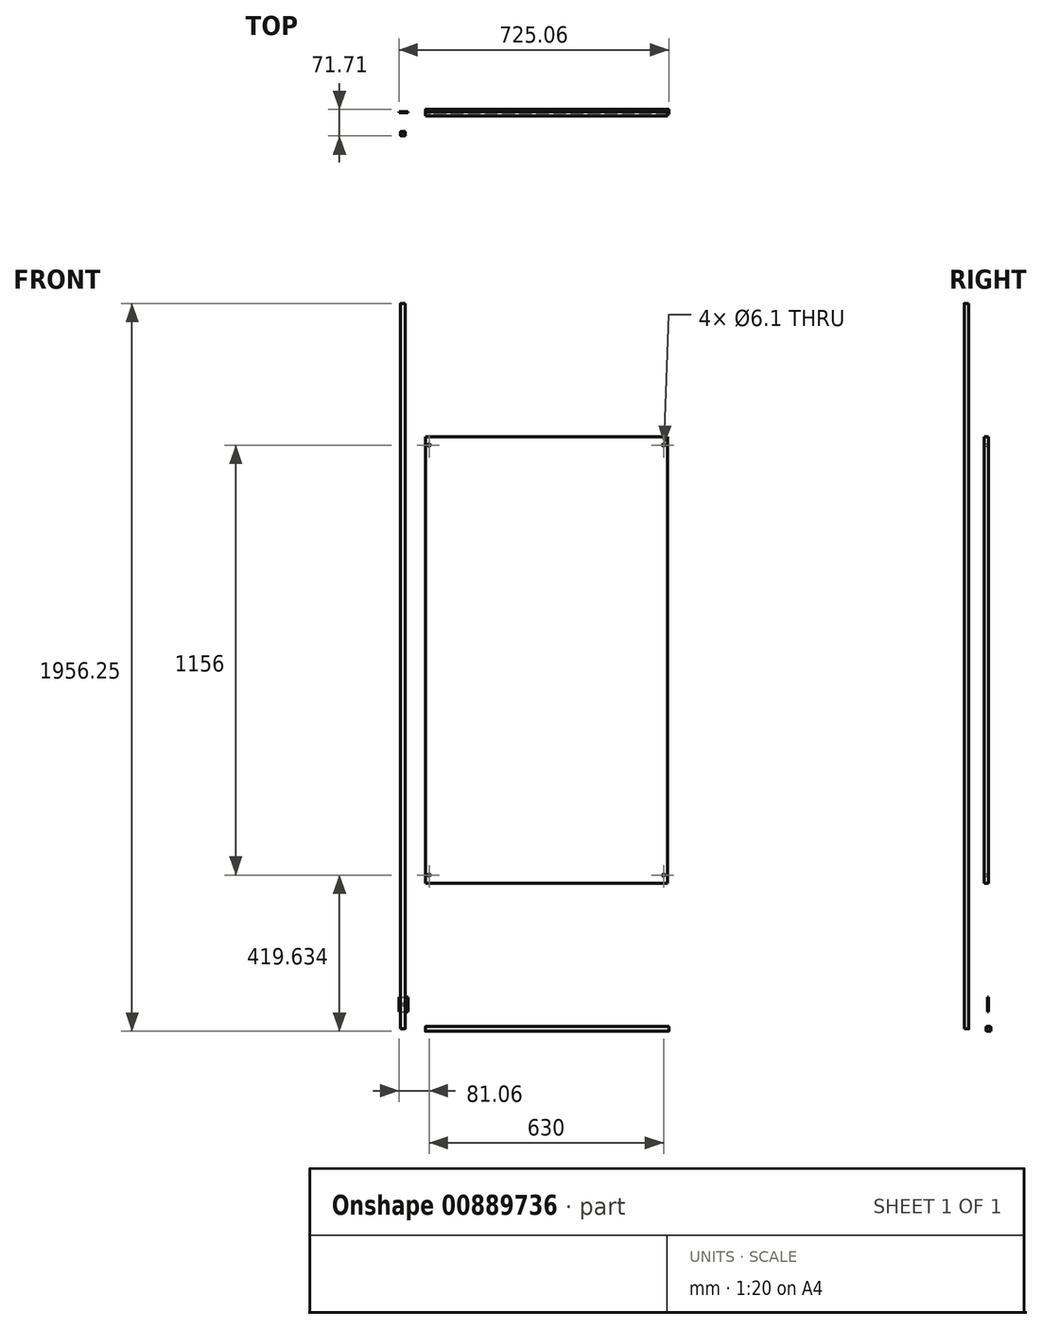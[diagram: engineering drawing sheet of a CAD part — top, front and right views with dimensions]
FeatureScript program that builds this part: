
annotation { "Feature Type Name" : "Feature", "Feature Type Description" : "" }
export const myFeature = defineFeature(function(context is Context, id is Id, definition is map)
    precondition{}
    {
        {
            var Q0;
            Q0=qCreatedBy(makeId("Top.planeOp"),FACE);
            var sketch = newSketch(context, id + "F0", { "sketchPlane" : qUnion([Q0])});
            skLineSegment(sketch, "E0.bottom", {"start": v(-64.96, -52.96) * mm, "end": v(-56.46, -52.96) * mm});
            skLineSegment(sketch, "E0.top", {"start": v(-64.96, -65.46) * mm, "end": v(-56.46, -65.46) * mm});
            skLineSegment(sketch, "E0.left", {"start": v(-66.96, -54.96) * mm, "end": v(-66.96, -63.46) * mm});
            skLineSegment(sketch, "E0.right", {"start": v(-54.46, -54.96) * mm, "end": v(-54.46, -63.46) * mm});
            skPoint(sketch, "E1.visualSharp", {"position": v(-66.96, -65.46) * mm});
            skArc(sketch, "E1.filletArc", {"start": v(-66.96, -63.46) * mm, "mid": v(-66.38, -64.88) * mm, "end": v(-64.96, -65.46) * mm});
            skPoint(sketch, "E2.visualSharp", {"position": v(-66.96, -52.96) * mm});
            skArc(sketch, "E2.filletArc", {"start": v(-64.96, -52.96) * mm, "mid": v(-66.38, -53.55) * mm, "end": v(-66.96, -54.96) * mm});
            skPoint(sketch, "E3.visualSharp", {"position": v(-54.46, -65.46) * mm});
            skArc(sketch, "E3.filletArc", {"start": v(-56.46, -65.46) * mm, "mid": v(-55.05, -64.88) * mm, "end": v(-54.46, -63.46) * mm});
            skPoint(sketch, "E4.visualSharp", {"position": v(-54.46, -52.96) * mm});
            skArc(sketch, "E4.filletArc", {"start": v(-54.46, -54.96) * mm, "mid": v(-55.05, -53.55) * mm, "end": v(-56.46, -52.96) * mm});
            skLineSegment(sketch, "E5.0", {"start": v(-65.76, -54.16) * mm, "end": v(-65.76, -64.26) * mm});
            skLineSegment(sketch, "E5.1", {"start": v(-65.76, -54.16) * mm, "end": v(-55.66, -54.16) * mm});
            skLineSegment(sketch, "E5.2", {"start": v(-55.66, -54.16) * mm, "end": v(-55.66, -64.26) * mm});
            skLineSegment(sketch, "E5.3", {"start": v(-65.76, -64.26) * mm, "end": v(-55.66, -64.26) * mm});
            skSolve(sketch);
        }
        {
            var Q0;
            Q0=makeQuery(id+"F0.imprint","IMPRINT",FACE,{"disambiguationData":[TD([[makeQuery(id+"F0.imprint","IMPRINT",EDGE,{"derivedFrom":sQuery(id+"F0.wireOp",EDGE,"E0.bottom")}),-1.0]])]});
            extrude(context, id + "F1", {"entities" : qUnion([Q0]), "depth" : 1950 * mm, "offsetDistance" : 25 * mm});
        }
        {
            var Q0;
            Q0=qCreatedBy(makeId("Right.planeOp"),FACE);
            var sketch = newSketch(context, id + "F2", { "sketchPlane" : qUnion([Q0])});
            skLineSegment(sketch, "E6.bottom", {"start": v(-4.25, 6.25) * mm, "end": v(4.25, 6.25) * mm});
            skLineSegment(sketch, "E6.top", {"start": v(-4.25, -6.25) * mm, "end": v(4.25, -6.25) * mm});
            skLineSegment(sketch, "E6.left", {"start": v(-6.25, 4.25) * mm, "end": v(-6.25, -4.25) * mm});
            skLineSegment(sketch, "E6.right", {"start": v(6.25, 4.25) * mm, "end": v(6.25, -4.25) * mm});
            skPoint(sketch, "E7.visualSharp", {"position": v(-6.25, -6.25) * mm});
            skArc(sketch, "E7.filletArc", {"start": v(-6.25, -4.25) * mm, "mid": v(-5.66, -5.66) * mm, "end": v(-4.25, -6.25) * mm});
            skPoint(sketch, "E8.visualSharp", {"position": v(-6.25, 6.25) * mm});
            skArc(sketch, "E8.filletArc", {"start": v(-4.25, 6.25) * mm, "mid": v(-5.66, 5.66) * mm, "end": v(-6.25, 4.25) * mm});
            skPoint(sketch, "E9.visualSharp", {"position": v(6.25, -6.25) * mm});
            skArc(sketch, "E9.filletArc", {"start": v(4.25, -6.25) * mm, "mid": v(5.66, -5.66) * mm, "end": v(6.25, -4.25) * mm});
            skPoint(sketch, "E10.visualSharp", {"position": v(6.25, 6.25) * mm});
            skArc(sketch, "E10.filletArc", {"start": v(6.25, 4.25) * mm, "mid": v(5.66, 5.66) * mm, "end": v(4.25, 6.25) * mm});
            skLineSegment(sketch, "E11.0", {"start": v(-5.05, 5.05) * mm, "end": v(-5.05, -5.05) * mm});
            skLineSegment(sketch, "E11.1", {"start": v(-5.05, 5.05) * mm, "end": v(5.05, 5.05) * mm});
            skLineSegment(sketch, "E11.2", {"start": v(5.05, 5.05) * mm, "end": v(5.05, -5.05) * mm});
            skLineSegment(sketch, "E11.3", {"start": v(-5.05, -5.05) * mm, "end": v(5.05, -5.05) * mm});
            skSolve(sketch);
        }
        {
            var Q0;
            Q0=makeQuery(id+"F2.imprint","IMPRINT",FACE,{"disambiguationData":[TD([[makeQuery(id+"F2.imprint","IMPRINT",EDGE,{"derivedFrom":sQuery(id+"F2.wireOp",EDGE,"E6.bottom")}),-1.0]])]});
            extrude(context, id + "F3", {"entities" : qUnion([Q0]), "depth" : 654 * mm, "offsetDistance" : 25 * mm});
        }
        {
            var Q0;
            Q0=qCreatedBy(makeId("Front.planeOp"),FACE);
            var sketch = newSketch(context, id + "F4", { "sketchPlane" : qUnion([Q0])});
            skLineSegment(sketch, "E12.bottom", {"start": v(-71.06, 85.54) * mm, "end": v(-47.06, 85.54) * mm});
            skLineSegment(sketch, "E12.top", {"start": v(-71.06, 45.54) * mm, "end": v(-47.06, 45.54) * mm});
            skLineSegment(sketch, "E12.left", {"start": v(-71.06, 85.54) * mm, "end": v(-71.06, 45.54) * mm});
            skLineSegment(sketch, "E12.right", {"start": v(-47.06, 85.54) * mm, "end": v(-47.06, 45.54) * mm});
            skPoint(sketch, "E13", {"position": v(-59.06, 65.54) * mm});
            skCircle(sketch, "E14", {"center": v(-59.06, 65.54) * mm, "radius": 3.1 * mm});
            skSolve(sketch);
        }
        {
            var Q0;
            Q0=makeQuery(id+"F4.imprint","IMPRINT",FACE,{"disambiguationData":[TD([[makeQuery(id+"F4.imprint","IMPRINT",EDGE,{"derivedFrom":sQuery(id+"F4.wireOp",EDGE,"E12.bottom")}),-1.0]])]});
            extrude(context, id + "F5", {"entities" : qUnion([Q0]), "depth" : 3 * mm, "offsetDistance" : 25 * mm});
        }
        {
            var Q0;
            Q0=qCreatedBy(makeId("Front.planeOp"),FACE);
            var sketch = newSketch(context, id + "F6", { "sketchPlane" : qUnion([Q0])});
            skLineSegment(sketch, "E15.bottom", {"start": v(0, 1591.38) * mm, "end": v(650, 1591.38) * mm});
            skLineSegment(sketch, "E15.top", {"start": v(0, 391.38) * mm, "end": v(650, 391.38) * mm});
            skLineSegment(sketch, "E15.left", {"start": v(0, 1591.38) * mm, "end": v(0, 391.38) * mm});
            skLineSegment(sketch, "E15.right", {"start": v(650, 1591.38) * mm, "end": v(650, 391.38) * mm});
            skPoint(sketch, "E16", {"position": v(10, 1569.38) * mm});
            skCircle(sketch, "E17", {"center": v(10, 1569.38) * mm, "radius": 3.05 * mm});
            skPoint(sketch, "E18", {"position": v(640, 1569.38) * mm});
            skPoint(sketch, "E19", {"position": v(640, 413.38) * mm});
            skPoint(sketch, "E20", {"position": v(10, 413.38) * mm});
            skCircle(sketch, "E21", {"center": v(640, 1569.38) * mm, "radius": 3.05 * mm});
            skCircle(sketch, "E22", {"center": v(640, 413.38) * mm, "radius": 3.05 * mm});
            skCircle(sketch, "E23", {"center": v(10, 413.38) * mm, "radius": 3.05 * mm});
            skSolve(sketch);
        }
        {
            var Q0;
            Q0 = qSketchRegion(id + "F6", true);
            var Q1;
            Q1=makeQuery(id+"F6.imprint","IMPRINT",FACE,{"disambiguationData":[TD([[makeQuery(id+"F6.imprint","IMPRINT",EDGE,{"derivedFrom":sQuery(id+"F6.wireOp",EDGE,"E15.bottom")}),-1.0]])]});
            extrude(context, id + "F7", {"entities" : qUnion([Q0, Q1]), "depth" : 12 * mm, "offsetDistance" : 25 * mm});
        }
    });
